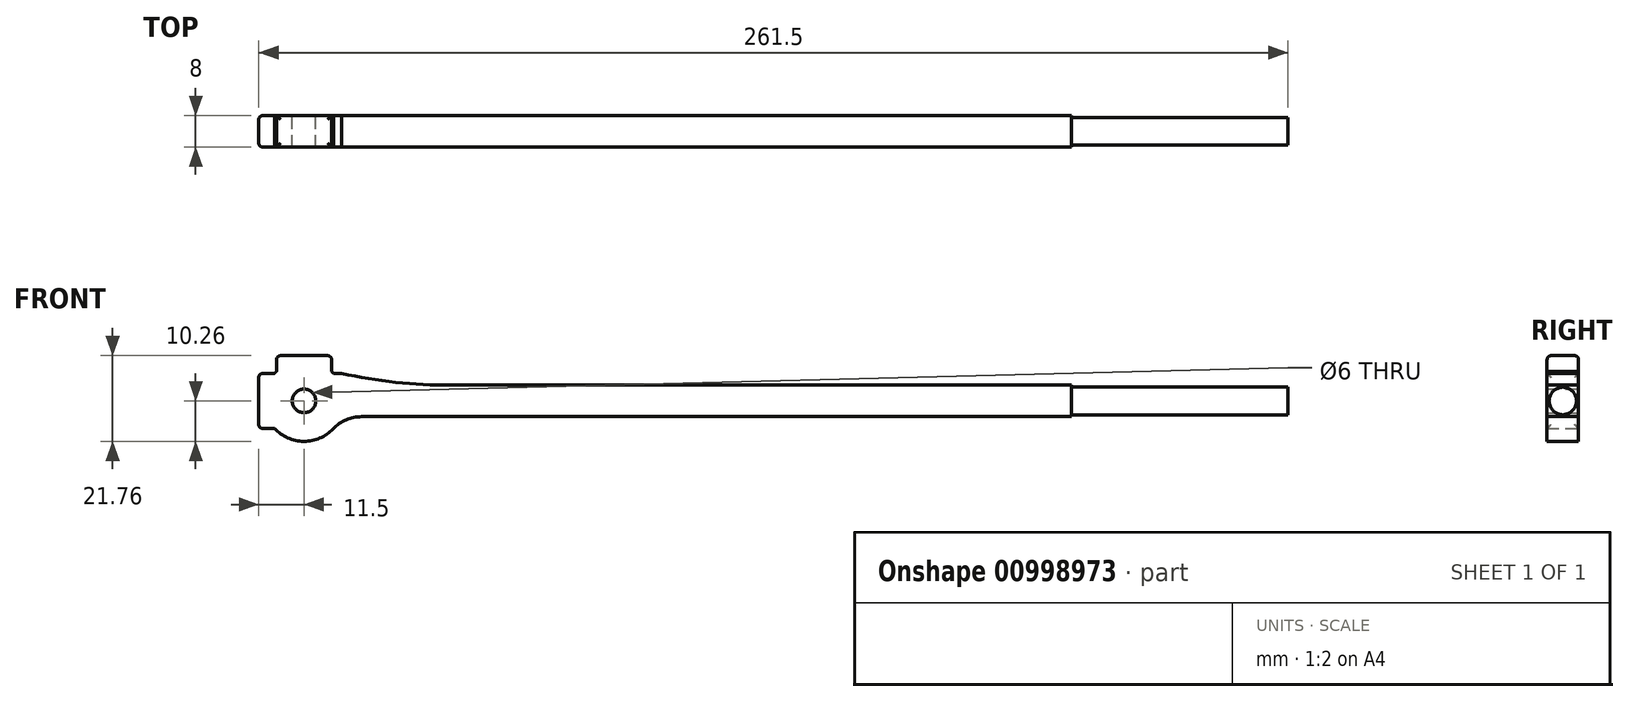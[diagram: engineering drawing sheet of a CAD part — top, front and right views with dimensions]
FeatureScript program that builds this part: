
annotation { "Feature Type Name" : "Feature", "Feature Type Description" : "" }
export const myFeature = defineFeature(function(context is Context, id is Id, definition is map)
    precondition{}
    {
        {
            var Q0;
            Q0=qCreatedBy(makeId("Front.planeOp"),FACE);
            var sketch = newSketch(context, id + "F0", { "sketchPlane" : qUnion([Q0])});
            skLineSegment(sketch, "E0.bottom", {"start": v(-11.5, 7) * mm, "end": v(-7.5, 7) * mm});
            skLineSegment(sketch, "E0.top", {"start": v(-11.5, -7) * mm, "end": v(-7.5, -7) * mm});
            skLineSegment(sketch, "E0.left", {"start": v(-11.5, 7) * mm, "end": v(-11.5, -7) * mm});
            skLineSegment(sketch, "E1.bottom", {"start": v(-7, 11.5) * mm, "end": v(7, 11.5) * mm});
            skLineSegment(sketch, "E1.left", {"start": v(-7, 11.5) * mm, "end": v(-7, 7.5) * mm});
            skLineSegment(sketch, "E1.right", {"start": v(7, 11.5) * mm, "end": v(7, 7.5) * mm});
            skPoint(sketch, "E2", {"position": v(0, 0) * mm});
            skCircle(sketch, "E3", {"center": v(0, 0) * mm, "radius": 3 * mm});
            skArc(sketch, "E4", {"start": v(-7, 7.5) * mm, "mid": v(-7.25, 7.25) * mm, "end": v(-7.5, 7) * mm});
            skLineSegment(sketch, "E5.trimOffspring", {"start": v(7.5, 7) * mm, "end": v(9.5, 7) * mm});
            skLineSegment(sketch, "E6", {"start": v(9.5, 7) * mm, "end": v(9.5, 4) * mm});
            skArc(sketch, "E7.trimOffspring", {"start": v(-7.5, -7) * mm, "mid": v(0, -10.26) * mm, "end": v(7.5, -7) * mm});
            skArc(sketch, "E8.trimOffspring", {"start": v(7.5, 7) * mm, "mid": v(7.25, 7.25) * mm, "end": v(7, 7.5) * mm});
            skLineSegment(sketch, "E9.bottom", {"start": v(9.5, 4) * mm, "end": v(195, 4) * mm});
            skLineSegment(sketch, "E9.top", {"start": v(9.5, -4) * mm, "end": v(195, -4) * mm});
            skArc(sketch, "E10.trimOffspring", {"start": v(-7.5, -7) * mm, "mid": v(1.79, -10.1) * mm, "end": v(9.45, -4) * mm});
            skLineSegment(sketch, "E11", {"start": v(9.5, -4) * mm, "end": v(9.45, -4) * mm});
            skLineSegment(sketch, "E12", {"start": v(195, 4) * mm, "end": v(195, -4) * mm});
            skSolve(sketch);
        }
        {
            var Q0;
            Q0 = qSketchRegion(id + "F0", true);
            extrude(context, id + "F1", {"entities" : qUnion([Q0]), "depth" : 8 * mm, "offsetDistance" : 25 * mm});
        }
        {
            var Q0;
            Q0=makeQuery(id+"F1.opExtrude","SWEPT_EDGE",EDGE,{"disambiguationData":[OSD([sQuery(id+"F0.wireOp",EDGE,"E10.trimOffspring"),sQuery(id+"F0.wireOp",EDGE,"E11")])]});
            fillet(context, id + "F2", {"entities" : qUnion([Q0]), "radius" : 10 * mm, "tangentPropagation" : true, "allowEdgeOverflow" : false});
        }
        {
            var Q0;
            Q0=makeQuery(id+"F1.opExtrude","SWEPT_EDGE",EDGE,{"disambiguationData":[OSD([sQuery(id+"F0.wireOp",EDGE,"E6"),sQuery(id+"F0.wireOp",EDGE,"E9.bottom")])]});
            fillet(context, id + "F3", {"entities" : qUnion([Q0]), "radius" : 130 * mm, "tangentPropagation" : true, "allowEdgeOverflow" : false});
        }
        {
            var Q0;
            Q0=makeQuery(id+"F1.opExtrude","SWEPT_FACE",FACE,{"disambiguationData":[OSD([sQuery(id+"F0.wireOp",EDGE,"E1.bottom")])]});
            var Q1;
            Q1=makeQuery(id+"F1.opExtrude","SWEPT_FACE",FACE,{"disambiguationData":[OSD([sQuery(id+"F0.wireOp",EDGE,"E0.left")])]});
            fillet(context, id + "F4", {"entities" : qUnion([Q0, Q1]), "radius" : 1 * mm, "tangentPropagation" : true, "allowEdgeOverflow" : false});
        }
        {
            var Q0;
            Q0=makeQuery(id+"F1.opExtrude","SWEPT_FACE",FACE,{"disambiguationData":[OSD([sQuery(id+"F0.wireOp",EDGE,"E12")])]});
            var sketch = newSketch(context, id + "F5", { "sketchPlane" : qUnion([Q0])});
            skCircle(sketch, "E13", {"center": v(-4, 0) * mm, "radius": 3.5 * mm});
            skSolve(sketch);
        }
        {
            var Q0;
            Q0=makeQuery(id+"F5.imprint","IMPRINT",FACE,{"disambiguationData":[TD([[makeQuery(id+"F5.imprint","IMPRINT",EDGE,{"derivedFrom":sQuery(id+"F5.wireOp",EDGE,"E13")}),1.0]])]});
            extrude(context, id + "F6", {"entities" : qUnion([Q0]), "operationType" : NewBodyOperationType.ADD, "depth" : 55 * mm, "offsetDistance" : 25 * mm});
        }
    });
